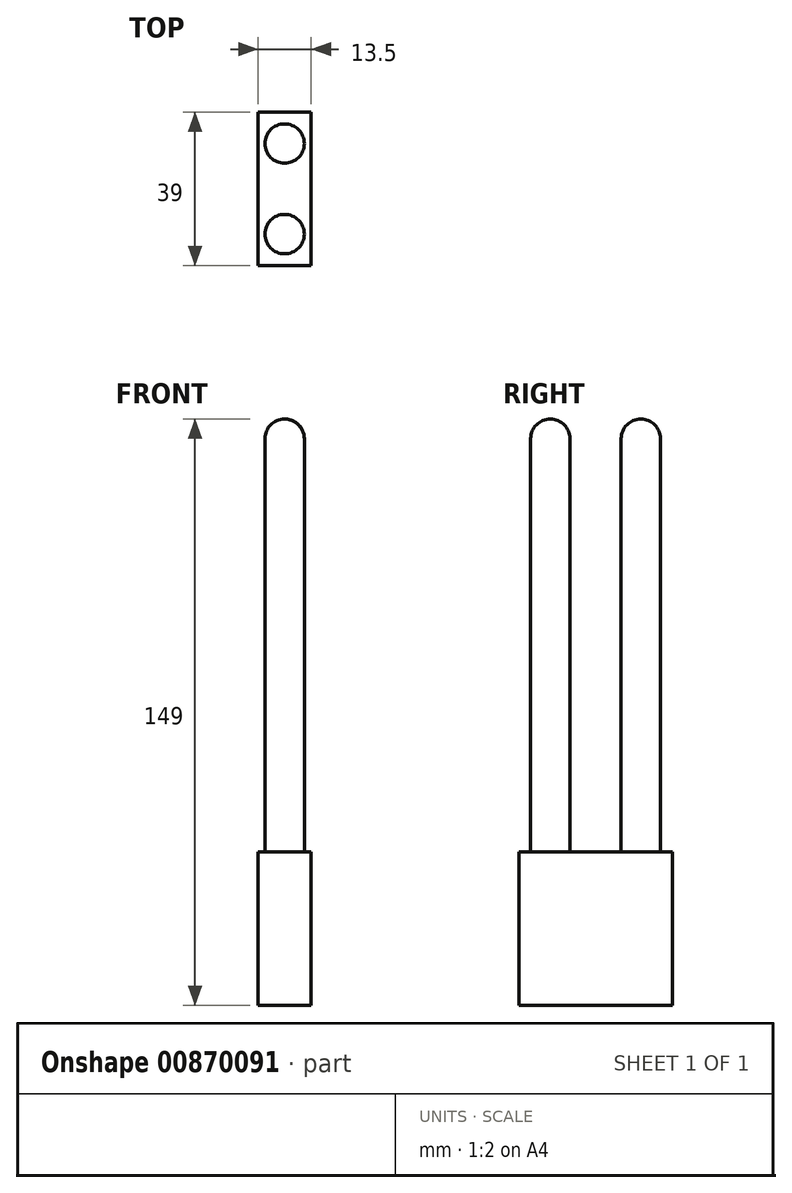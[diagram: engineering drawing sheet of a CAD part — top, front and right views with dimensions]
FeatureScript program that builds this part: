
annotation { "Feature Type Name" : "Feature", "Feature Type Description" : "" }
export const myFeature = defineFeature(function(context is Context, id is Id, definition is map)
    precondition{}
    {
        {
            var Q0;
            Q0=qCreatedBy(makeId("Right.planeOp"),FACE);
            var sketch = newSketch(context, id + "F0", { "sketchPlane" : qUnion([Q0])});
            skLineSegment(sketch, "E0.bottom", {"start": v(19.5, 19.5) * mm, "end": v(-19.5, 19.5) * mm});
            skLineSegment(sketch, "E0.top", {"start": v(19.5, -19.5) * mm, "end": v(-19.5, -19.5) * mm});
            skLineSegment(sketch, "E0.left", {"start": v(19.5, 19.5) * mm, "end": v(19.5, -19.5) * mm});
            skLineSegment(sketch, "E0.right", {"start": v(-19.5, 19.5) * mm, "end": v(-19.5, -19.5) * mm});
            skPoint(sketch, "E0.middle", {"position": v(0, 0) * mm});
            skSolve(sketch);
        }
        {
            var Q0;
            Q0=makeQuery(id+"F0.imprint","IMPRINT",FACE,{"disambiguationData":[TD([[makeQuery(id+"F0.imprint","IMPRINT",EDGE,{"derivedFrom":sQuery(id+"F0.wireOp",EDGE,"E0.bottom")}),1.0]])]});
            extrude(context, id + "F1", {"entities" : qUnion([Q0]), "depth" : 13.5 * mm, "offsetDistance" : 25 * mm});
        }
        {
            var Q0;
            Q0=makeQuery(id+"F1.opExtrude","SWEPT_FACE",FACE,{"disambiguationData":[OSD([sQuery(id+"F0.wireOp",EDGE,"E0.bottom")])]});
            var sketch = newSketch(context, id + "F2", { "sketchPlane" : qUnion([Q0])});
            skLineSegment(sketch, "E1", {"start": v(0, 19.5) * mm, "end": v(0, 16.5) * mm, "construction": true});
            skLineSegment(sketch, "E2", {"start": v(0, -19.5) * mm, "end": v(0, -16.5) * mm, "construction": true});
            skLineSegment(sketch, "E3", {"start": v(0, 16.5) * mm, "end": v(13.5, 16.5) * mm, "construction": true});
            skLineSegment(sketch, "E4", {"start": v(0, -16.5) * mm, "end": v(13.5, -16.5) * mm, "construction": true});
            skLineSegment(sketch, "E5", {"start": v(0, 16.5) * mm, "end": v(0, 11.5) * mm, "construction": true});
            skLineSegment(sketch, "E6", {"start": v(0, -16.5) * mm, "end": v(0, -11.5) * mm, "construction": true});
            skLineSegment(sketch, "E7", {"start": v(0, 11.5) * mm, "end": v(13.5, 11.5) * mm, "construction": true});
            skLineSegment(sketch, "E8", {"start": v(0, -11.5) * mm, "end": v(13.5, -11.5) * mm, "construction": true});
            skCircle(sketch, "E9", {"center": v(6.75, 11.5) * mm, "radius": 5 * mm});
            skCircle(sketch, "E10", {"center": v(6.75, -11.5) * mm, "radius": 5 * mm});
            skSolve(sketch);
        }
        {
            var Q0;
            Q0=makeQuery(id+"F2.imprint","IMPRINT",FACE,{"disambiguationData":[TD([[makeQuery(id+"F2.imprint","IMPRINT",EDGE,{"derivedFrom":sQuery(id+"F2.wireOp",EDGE,"E9")}),1.0]])]});
            var Q1;
            Q1=makeQuery(id+"F2.imprint","IMPRINT",FACE,{"disambiguationData":[TD([[makeQuery(id+"F2.imprint","IMPRINT",EDGE,{"derivedFrom":sQuery(id+"F2.wireOp",EDGE,"E10")}),1.0]])]});
            extrude(context, id + "F3", {"entities" : qUnion([Q0, Q1]), "operationType" : NewBodyOperationType.ADD, "depth" : 110 * mm, "offsetDistance" : 25 * mm});
        }
        {
            var Q0;
            Q0=makeQuery(id+"F3.opExtrude","CAP_EDGE",EDGE,{"disambiguationData":[OSD([sQuery(id+"F2.wireOp",EDGE,"E9")])],"isStart":false});
            var Q1;
            Q1=makeQuery(id+"F3.opExtrude","CAP_EDGE",EDGE,{"disambiguationData":[OSD([sQuery(id+"F2.wireOp",EDGE,"E10")])],"isStart":false});
            fillet(context, id + "F4", {"entities" : qUnion([Q0, Q1]), "radius" : 5 * mm, "tangentPropagation" : true, "allowEdgeOverflow" : false});
        }
    });
